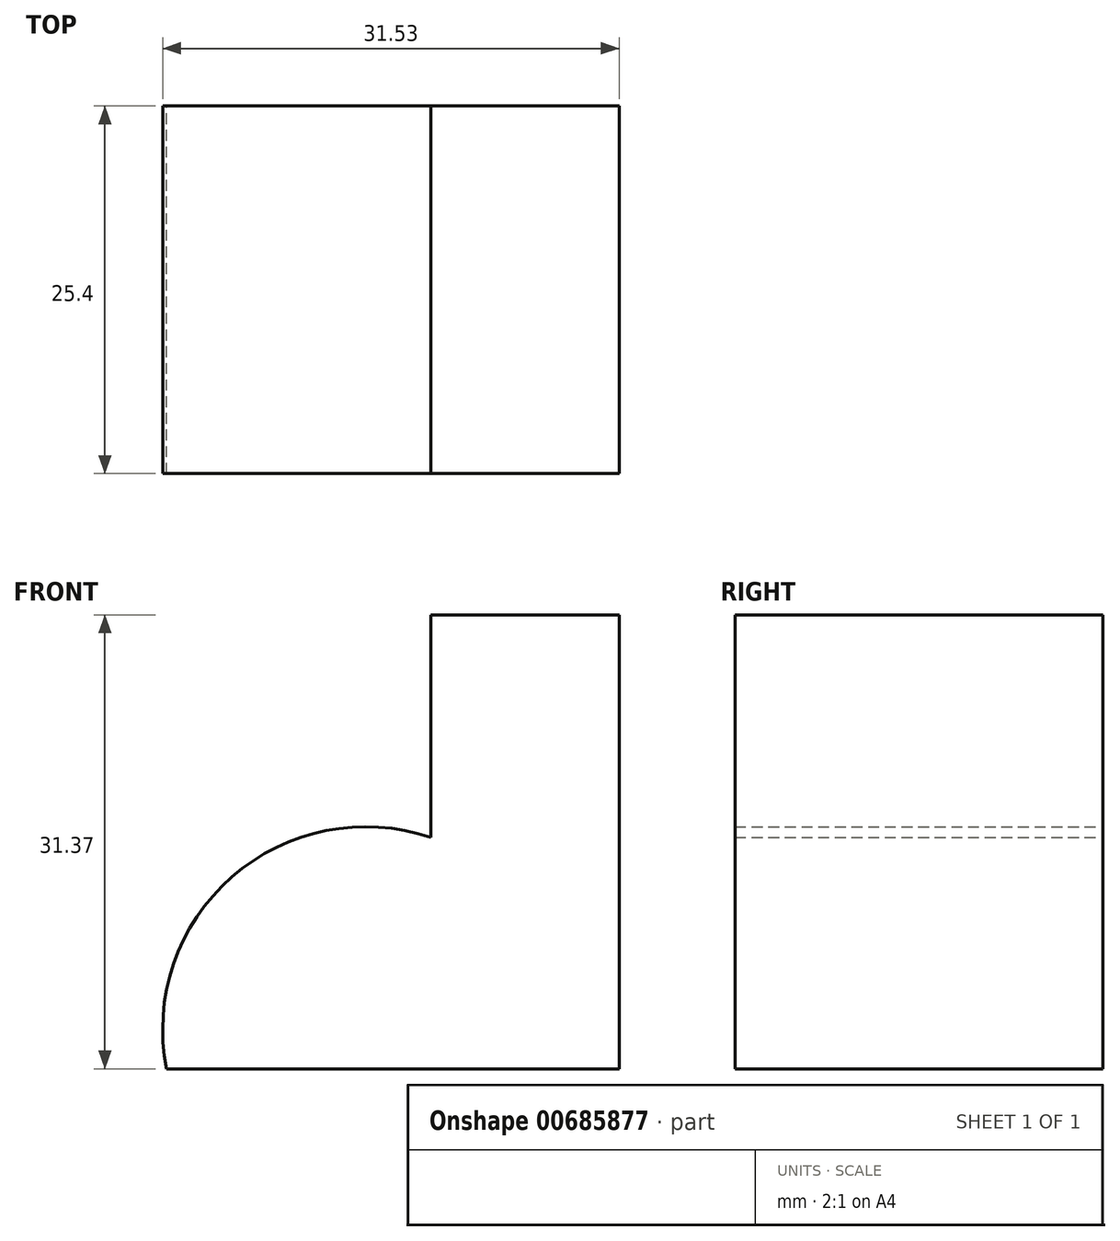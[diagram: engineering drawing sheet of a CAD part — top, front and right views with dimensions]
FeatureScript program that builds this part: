
annotation { "Feature Type Name" : "Feature", "Feature Type Description" : "" }
export const myFeature = defineFeature(function(context is Context, id is Id, definition is map)
    precondition{}
    {
        {
            var Q0;
            Q0=qCreatedBy(makeId("Front.planeOp"),FACE);
            var sketch = newSketch(context, id + "F0", { "sketchPlane" : qUnion([Q0])});
            skLineSegment(sketch, "E0", {"start": v(0, 0) * mm, "end": v(31.27, 0) * mm});
            skLineSegment(sketch, "E1", {"start": v(31.27, 0) * mm, "end": v(31.27, 31.37) * mm});
            skLineSegment(sketch, "E2", {"start": v(31.27, 31.37) * mm, "end": v(18.25, 31.37) * mm});
            skLineSegment(sketch, "E3", {"start": v(18.25, 31.37) * mm, "end": v(18.25, 15.98) * mm});
            skArc(sketch, "E4", {"start": v(18.25, 15.98) * mm, "mid": v(4.52, 13.25) * mm, "end": v(0, 0) * mm});
            skSolve(sketch);
        }
        {
            var Q0;
            Q0 = qSketchRegion(id + "F0", true);
            extrude(context, id + "F1", {"entities" : qUnion([Q0]), "depth" : 25.4 * mm, "offsetDistance" : 25.4 * mm});
        }
    });
